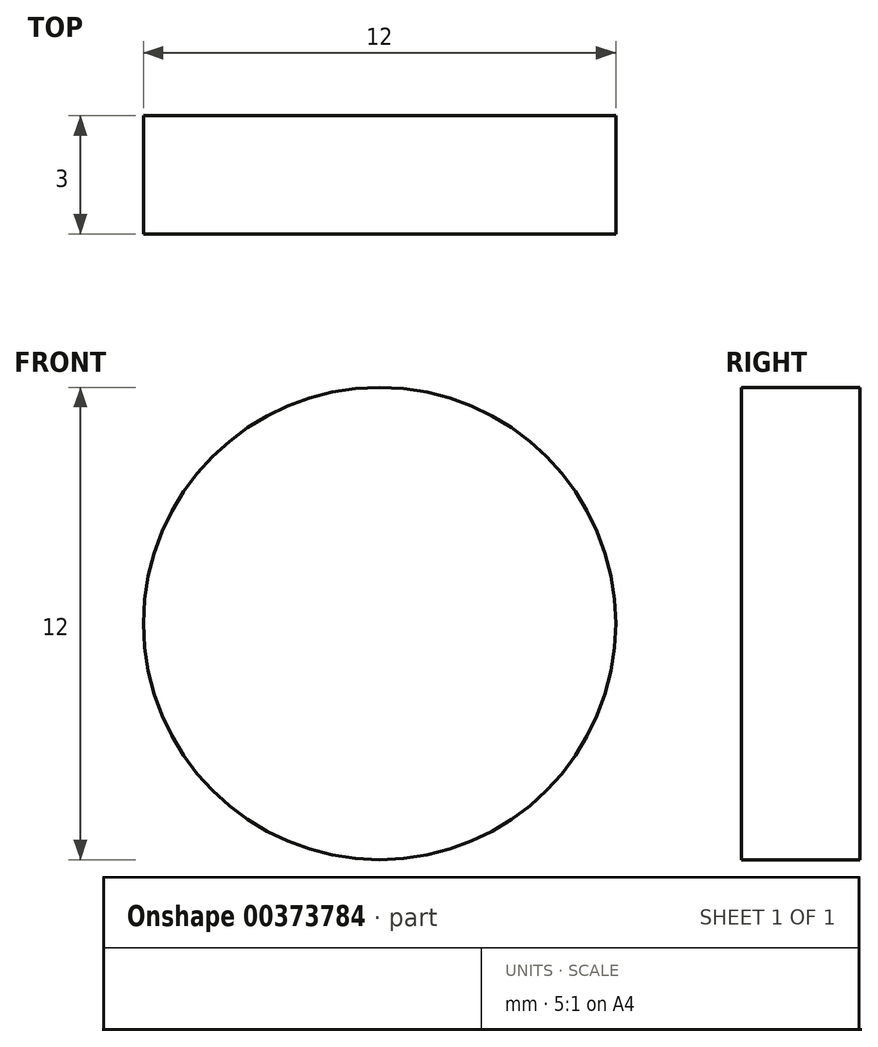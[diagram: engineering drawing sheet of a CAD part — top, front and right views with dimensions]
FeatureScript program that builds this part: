
annotation { "Feature Type Name" : "Feature", "Feature Type Description" : "" }
export const myFeature = defineFeature(function(context is Context, id is Id, definition is map)
    precondition{}
    {
        {
            var Q0;
            Q0=qCreatedBy(makeId("Front.planeOp"),FACE);
            var sketch = newSketch(context, id + "F0", { "sketchPlane" : qUnion([Q0])});
            skCircle(sketch, "E0", {"center": v(0, 0) * mm, "radius": 6 * mm});
            skSolve(sketch);
        }
        {
            var Q0;
            Q0=qSketchRegion(id+"F0",true);
            extrude(context, id + "F1", {"entities" : qUnion([Q0]), "depth" : 3 * mm});
        }
    });
